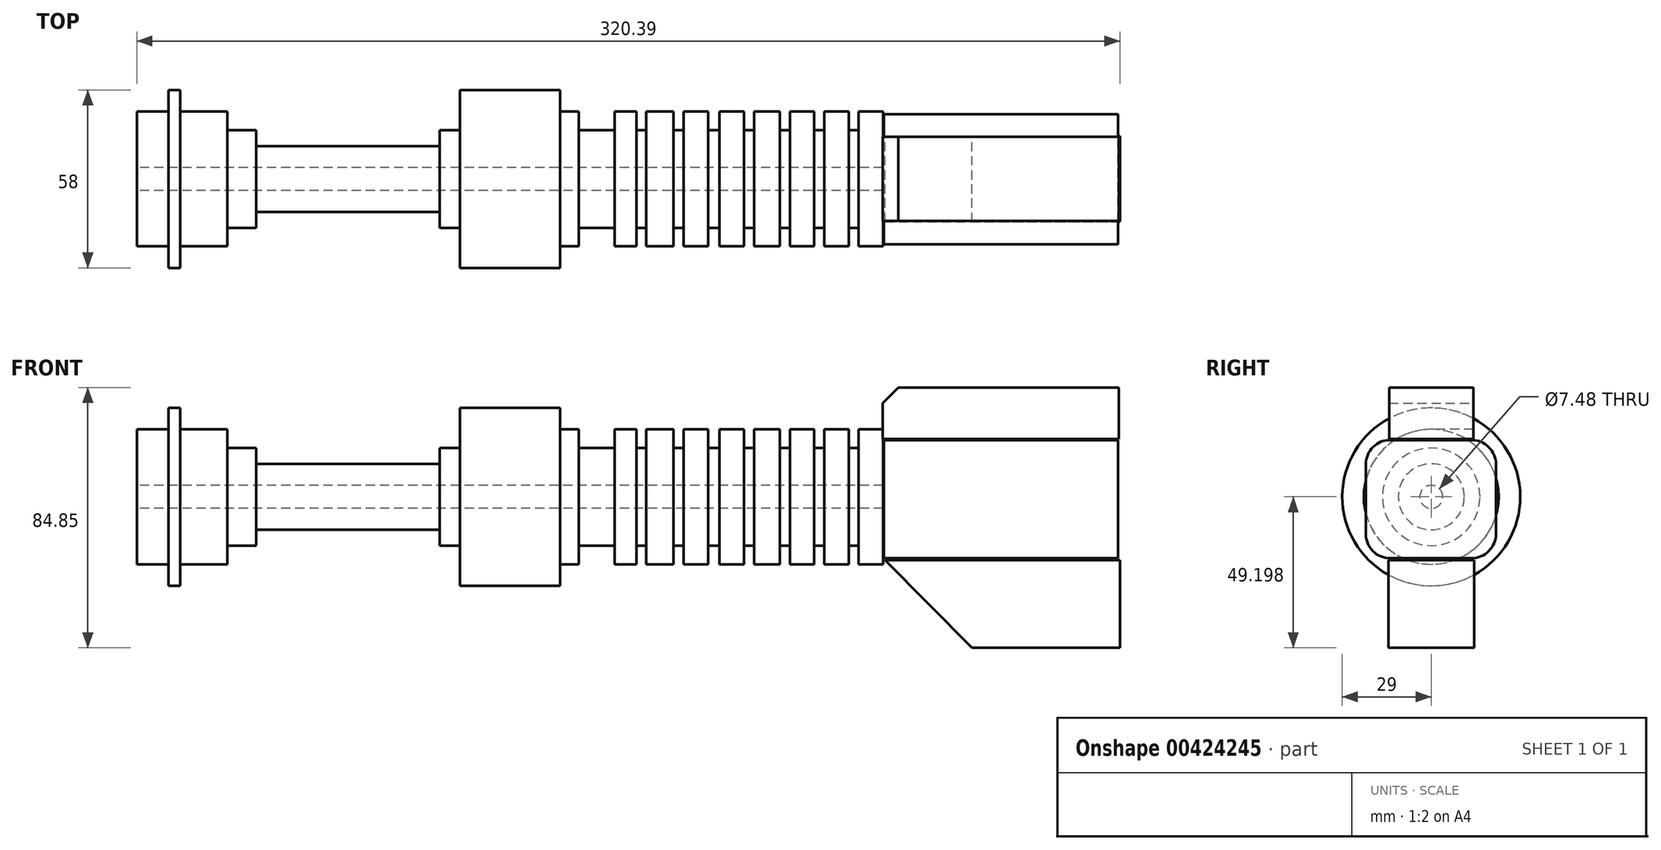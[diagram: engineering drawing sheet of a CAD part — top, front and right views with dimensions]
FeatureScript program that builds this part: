
annotation { "Feature Type Name" : "Feature", "Feature Type Description" : "" }
export const myFeature = defineFeature(function(context is Context, id is Id, definition is map)
    precondition{}
    {
        {
            var Q0;
            Q0=qCreatedBy(makeId("Front.planeOp"),FACE);
            var sketch = newSketch(context, id + "F0", { "sketchPlane" : qUnion([Q0])});
            skLineSegment(sketch, "E0", {"start": v(-174.92, 0) * mm, "end": v(0, 0) * mm});
            skLineSegment(sketch, "E1", {"start": v(-174.92, 0) * mm, "end": v(-174.92, 18.24) * mm});
            skLineSegment(sketch, "E2", {"start": v(-174.92, 18.24) * mm, "end": v(-164.63, 18.24) * mm});
            skLineSegment(sketch, "E3", {"start": v(-164.63, 18.24) * mm, "end": v(-164.63, 25.26) * mm});
            skLineSegment(sketch, "E4", {"start": v(-164.63, 25.26) * mm, "end": v(-160.89, 25.26) * mm});
            skLineSegment(sketch, "E5", {"start": v(-160.89, 25.26) * mm, "end": v(-160.89, 18.24) * mm});
            skLineSegment(sketch, "E6", {"start": v(-160.89, 18.24) * mm, "end": v(-145.45, 18.24) * mm});
            skLineSegment(sketch, "E7", {"start": v(-145.45, 18.24) * mm, "end": v(-145.45, 12.16) * mm});
            skLineSegment(sketch, "E8", {"start": v(-145.45, 12.16) * mm, "end": v(-136.1, 12.16) * mm});
            skLineSegment(sketch, "E9", {"start": v(-136.1, 12.16) * mm, "end": v(-136.1, 7.02) * mm});
            skLineSegment(sketch, "E10", {"start": v(-136.1, 7.02) * mm, "end": v(-76.23, 7.02) * mm});
            skLineSegment(sketch, "E11", {"start": v(-76.23, 7.02) * mm, "end": v(-76.23, 12.16) * mm});
            skLineSegment(sketch, "E12", {"start": v(-76.23, 12.16) * mm, "end": v(-69.69, 12.16) * mm});
            skLineSegment(sketch, "E13", {"start": v(-69.69, 12.16) * mm, "end": v(-69.69, 25.26) * mm});
            skLineSegment(sketch, "E14", {"start": v(-69.69, 25.26) * mm, "end": v(-36.95, 25.26) * mm});
            skLineSegment(sketch, "E15", {"start": v(-36.95, 25.26) * mm, "end": v(-36.95, 18.24) * mm});
            skLineSegment(sketch, "E16", {"start": v(-36.95, 18.24) * mm, "end": v(-30.87, 18.24) * mm});
            skLineSegment(sketch, "E17", {"start": v(-30.87, 18.24) * mm, "end": v(-30.87, 12.16) * mm});
            skLineSegment(sketch, "E18", {"start": v(-30.87, 12.16) * mm, "end": v(-19.18, 12.16) * mm});
            skLineSegment(sketch, "E19", {"start": v(-19.18, 12.16) * mm, "end": v(-19.18, 18.24) * mm});
            skLineSegment(sketch, "E20", {"start": v(-19.18, 18.24) * mm, "end": v(-12.16, 18.24) * mm});
            skLineSegment(sketch, "E21", {"start": v(-12.16, 18.24) * mm, "end": v(-12.16, 12.16) * mm});
            skLineSegment(sketch, "E22", {"start": v(-12.16, 12.16) * mm, "end": v(-8.89, 12.16) * mm});
            skLineSegment(sketch, "E23", {"start": v(-8.89, 12.16) * mm, "end": v(-8.89, 18.24) * mm});
            skLineSegment(sketch, "E24", {"start": v(-8.89, 18.24) * mm, "end": v(0, 18.24) * mm});
            skLineSegment(sketch, "E25", {"start": v(0, 18.24) * mm, "end": v(0, 12.16) * mm});
            skLineSegment(sketch, "E26", {"start": v(0, 12.16) * mm, "end": v(3.27, 12.16) * mm});
            skLineSegment(sketch, "E27", {"start": v(3.27, 12.16) * mm, "end": v(3.27, 18.24) * mm});
            skLineSegment(sketch, "E28", {"start": v(3.27, 18.24) * mm, "end": v(11.22, 18.24) * mm});
            skLineSegment(sketch, "E29", {"start": v(11.22, 18.24) * mm, "end": v(11.22, 12.16) * mm});
            skLineSegment(sketch, "E30", {"start": v(11.22, 12.16) * mm, "end": v(14.97, 12.16) * mm});
            skLineSegment(sketch, "E31", {"start": v(14.97, 12.16) * mm, "end": v(14.97, 18.24) * mm});
            skLineSegment(sketch, "E32", {"start": v(14.97, 18.24) * mm, "end": v(22.92, 18.24) * mm});
            skLineSegment(sketch, "E33", {"start": v(22.92, 18.24) * mm, "end": v(22.92, 12.16) * mm});
            skLineSegment(sketch, "E34", {"start": v(22.92, 12.16) * mm, "end": v(26.2, 12.16) * mm});
            skLineSegment(sketch, "E35", {"start": v(26.2, 12.16) * mm, "end": v(26.2, 18.24) * mm});
            skLineSegment(sketch, "E36", {"start": v(26.2, 18.24) * mm, "end": v(34.6, 18.24) * mm});
            skLineSegment(sketch, "E37", {"start": v(34.6, 18.24) * mm, "end": v(34.6, 12.16) * mm});
            skLineSegment(sketch, "E38", {"start": v(34.6, 12.16) * mm, "end": v(37.88, 12.16) * mm});
            skLineSegment(sketch, "E39", {"start": v(37.88, 12.16) * mm, "end": v(37.88, 18.24) * mm});
            skLineSegment(sketch, "E40", {"start": v(37.88, 18.24) * mm, "end": v(45.83, 18.24) * mm});
            skLineSegment(sketch, "E41", {"start": v(45.83, 18.24) * mm, "end": v(45.83, 12.16) * mm});
            skLineSegment(sketch, "E42", {"start": v(45.83, 12.16) * mm, "end": v(49.1, 12.16) * mm});
            skLineSegment(sketch, "E43", {"start": v(49.1, 12.16) * mm, "end": v(49.1, 18.24) * mm});
            skLineSegment(sketch, "E44", {"start": v(49.1, 18.24) * mm, "end": v(57.06, 18.24) * mm});
            skLineSegment(sketch, "E45", {"start": v(57.06, 18.24) * mm, "end": v(57.06, 12.16) * mm});
            skLineSegment(sketch, "E46", {"start": v(57.06, 12.16) * mm, "end": v(60.33, 12.16) * mm});
            skLineSegment(sketch, "E47", {"start": v(60.33, 12.16) * mm, "end": v(60.33, 18.24) * mm});
            skLineSegment(sketch, "E48", {"start": v(60.33, 18.24) * mm, "end": v(68.28, 18.24) * mm});
            skLineSegment(sketch, "E49", {"start": v(68.28, 18.24) * mm, "end": v(68.28, 12.16) * mm});
            skLineSegment(sketch, "E50", {"start": v(68.28, 12.16) * mm, "end": v(68.28, 0) * mm});
            skLineSegment(sketch, "E51", {"start": v(68.28, 0) * mm, "end": v(0, 0) * mm});
            skLineSegment(sketch, "E52", {"start": v(0, 0) * mm, "end": v(68.28, 0) * mm});
            skLineSegment(sketch, "E53", {"start": v(68.28, 0) * mm, "end": v(-174.92, 0) * mm});
            skLineSegment(sketch, "E54", {"start": v(-192.22, -3.74) * mm, "end": v(98.68, -3.74) * mm});
            skSolve(sketch);
        }
        {
            var Q0;
            {var subQ0=sQuery(id+"F0.wireOp",EDGE,"E1");Q0=makeQuery(id+"F0.imprint","IMPRINT",FACE,{"disambiguationData":[TD([[makeQuery(id+"F0.imprint","IMPRINT",EDGE,{"derivedFrom":subQ0}),-1.0]])]});}
            var Q1;
            Q1=sQuery(id+"F0.wireOp",EDGE,"E54");
            revolve(context, id + "F1", {"entities" : qUnion([Q0]), "axis" : qUnion([Q1]), "revolveType" : RevolveType.FULL});
        }
        {
            var Q0;
            Q0=qCreatedBy(makeId("Front.planeOp"),FACE);
            var sketch = newSketch(context, id + "F2", { "sketchPlane" : qUnion([Q0])});
            skLineSegment(sketch, "E55.bottom", {"start": v(68.52, 11.23) * mm, "end": v(144.82, 11.23) * mm});
            skLineSegment(sketch, "E55.top", {"start": v(68.52, -18.2) * mm, "end": v(144.82, -18.2) * mm});
            skLineSegment(sketch, "E55.left", {"start": v(68.52, 11.23) * mm, "end": v(68.52, -18.2) * mm});
            skLineSegment(sketch, "E55.right", {"start": v(144.82, 11.23) * mm, "end": v(144.82, -18.2) * mm});
            skSolve(sketch);
        }
        {
            var Q0;
            Q0 = qSketchRegion(id + "F2", true);
            extrude(context, id + "F3", {"entities" : qUnion([Q0]), "depth" : 21.34 * mm});
        }
        {
            var Q0;
            Q0=makeQuery(id+"F3.opExtrude","CAP_FACE",FACE,{"disambiguationData":[OSD([sQuery(id+"F2.wireOp",EDGE,"E55.bottom"),sQuery(id+"F2.wireOp",EDGE,"E55.top"),sQuery(id+"F2.wireOp",EDGE,"E55.left"),sQuery(id+"F2.wireOp",EDGE,"E55.right")])],"isStart":true});
            extrude(context, id + "F4", {"entities" : qUnion([Q0]), "operationType" : NewBodyOperationType.ADD, "depth" : 21.08 * mm});
        }
        {
            var Q0;
            {var subQ0=sQuery(id+"F2.wireOp",EDGE,"E55.bottom");Q0=makeQuery(id+"F4.boolean.opBoolean","MERGE",FACE,{"derivedFrom":[makeQuery(id+"F3.opExtrude","SWEPT_FACE",FACE,{"disambiguationData":[OSD([subQ0])]}),makeQuery(id+"F4.opExtrude","SWEPT_FACE",FACE,{"disambiguationData":[OSD([subQ0])]})]});}
            extrude(context, id + "F5", {"entities" : qUnion([Q0]), "operationType" : NewBodyOperationType.ADD, "depth" : 3.56 * mm});
        }
        {
            var Q0;
            {var subQ0=sQuery(id+"F2.wireOp",EDGE,"E55.top");Q0=makeQuery(id+"F4.boolean.opBoolean","MERGE",FACE,{"derivedFrom":[makeQuery(id+"F3.opExtrude","SWEPT_FACE",FACE,{"disambiguationData":[OSD([subQ0])]}),makeQuery(id+"F4.opExtrude","SWEPT_FACE",FACE,{"disambiguationData":[OSD([subQ0])]})]});}
            extrude(context, id + "F6", {"entities" : qUnion([Q0]), "operationType" : NewBodyOperationType.ADD, "depth" : 5.6 * mm});
        }
        {
            var Q0;
            {var subQ0=sQuery(id+"F2.wireOp",EDGE,"E55.top");Q0=makeQuery(id+"F6.opExtrude","CAP_EDGE",EDGE,{"disambiguationData":[OSD([subQ0]),TDD([makeQuery(id+"F3.opExtrude","CAP_EDGE",EDGE,{"disambiguationData":[OSD([subQ0])],"isStart":false})])],"isStart":false});}
            fillet(context, id + "F7", {"entities" : qUnion([Q0]), "radius" : 7.97 * mm, "tangentPropagation" : true, "allowEdgeOverflow" : false});
        }
        {
            var Q0;
            {var subQ0=sQuery(id+"F2.wireOp",EDGE,"E55.bottom");Q0=makeQuery(id+"F5.opExtrude","CAP_EDGE",EDGE,{"disambiguationData":[OSD([subQ0]),TDD([makeQuery(id+"F3.opExtrude","CAP_EDGE",EDGE,{"disambiguationData":[OSD([subQ0])],"isStart":false})])],"isStart":false});}
            fillet(context, id + "F8", {"entities" : qUnion([Q0]), "radius" : 7.98 * mm, "tangentPropagation" : true, "allowEdgeOverflow" : false});
        }
        {
            var Q0;
            {var subQ0=sQuery(id+"F2.wireOp",EDGE,"E55.bottom");Q0=makeQuery(id+"F5.opExtrude","CAP_EDGE",EDGE,{"disambiguationData":[OSD([subQ0]),TDD([makeQuery(id+"F4.opExtrude","CAP_EDGE",EDGE,{"disambiguationData":[OSD([subQ0])],"isStart":false})])],"isStart":false});}
            fillet(context, id + "F9", {"entities" : qUnion([Q0]), "radius" : 7.98 * mm, "tangentPropagation" : true, "allowEdgeOverflow" : false});
        }
        {
            var Q0;
            {var subQ0=sQuery(id+"F2.wireOp",EDGE,"E55.top");Q0=makeQuery(id+"F6.opExtrude","CAP_EDGE",EDGE,{"disambiguationData":[OSD([subQ0]),TDD([makeQuery(id+"F4.opExtrude","CAP_EDGE",EDGE,{"disambiguationData":[OSD([subQ0])],"isStart":false})])],"isStart":false});}
            fillet(context, id + "F10", {"entities" : qUnion([Q0]), "radius" : 7.98 * mm, "tangentPropagation" : true, "allowEdgeOverflow" : false});
        }
        {
            var Q0;
            Q0=qCreatedBy(makeId("Front.planeOp"),FACE);
            var sketch = newSketch(context, id + "F11", { "sketchPlane" : qUnion([Q0])});
            skLineSegment(sketch, "E56.bottom", {"start": v(68.2, 15.1) * mm, "end": v(145.12, 15.1) * mm});
            skLineSegment(sketch, "E56.top", {"start": v(68.2, 31.9) * mm, "end": v(145.12, 31.9) * mm});
            skLineSegment(sketch, "E56.left", {"start": v(68.2, 15.1) * mm, "end": v(68.2, 31.9) * mm});
            skLineSegment(sketch, "E56.right", {"start": v(145.12, 15.1) * mm, "end": v(145.12, 31.9) * mm});
            skSolve(sketch);
        }
        {
            var Q0;
            Q0=makeQuery(id+"F11.imprint","IMPRINT",FACE,{"disambiguationData":[TD([[makeQuery(id+"F11.imprint","IMPRINT",EDGE,{"derivedFrom":sQuery(id+"F11.wireOp",EDGE,"E56.bottom")}),1.0]])]});
            extrude(context, id + "F12", {"entities" : qUnion([Q0]), "operationType" : NewBodyOperationType.ADD, "depth" : 13.72 * mm});
        }
        {
            var Q0;
            Q0=makeQuery(id+"F12.opExtrude","CAP_FACE",FACE,{"disambiguationData":[OSD([sQuery(id+"F11.wireOp",EDGE,"E56.bottom"),sQuery(id+"F11.wireOp",EDGE,"E56.top"),sQuery(id+"F11.wireOp",EDGE,"E56.left"),sQuery(id+"F11.wireOp",EDGE,"E56.right")])],"isStart":true});
            extrude(context, id + "F13", {"entities" : qUnion([Q0]), "operationType" : NewBodyOperationType.ADD, "depth" : 13.72 * mm});
        }
        {
            var Q0;
            {var subQ0=sQuery(id+"F11.wireOp",EDGE,"E56.left");var subQ1=sQuery(id+"F11.wireOp",EDGE,"E56.top");Q0=makeQuery(id+"F13.boolean.opBoolean","MERGE",EDGE,{"derivedFrom":[makeQuery(id+"F12.opExtrude","SWEPT_EDGE",EDGE,{"disambiguationData":[OSD([subQ1,subQ0])]}),makeQuery(id+"F13.opExtrude","SWEPT_EDGE",EDGE,{"disambiguationData":[OSD([subQ1,subQ0])]})]});}
            chamfer(context, id + "F14", {"entities" : qUnion([Q0]), "width" : 5.08 * mm, "tangentPropagation" : true});
        }
        {
            var Q0;
            Q0=qCreatedBy(makeId("Front.planeOp"),FACE);
            var sketch = newSketch(context, id + "F15", { "sketchPlane" : qUnion([Q0])});
            skLineSegment(sketch, "E57", {"start": v(68.97, -24.34) * mm, "end": v(97.2, -52.94) * mm});
            skLineSegment(sketch, "E58", {"start": v(97.2, -52.94) * mm, "end": v(145.47, -52.94) * mm});
            skLineSegment(sketch, "E59", {"start": v(145.47, -52.94) * mm, "end": v(145.47, 14.62) * mm});
            skLineSegment(sketch, "E60", {"start": v(68.97, -24.34) * mm, "end": v(145.47, -24.34) * mm});
            skSolve(sketch);
        }
        {
            var Q0;
            Q0=makeQuery(id+"F15.imprint","IMPRINT",FACE,{"disambiguationData":[TD([[makeQuery(id+"F15.imprint","IMPRINT",EDGE,{"derivedFrom":sQuery(id+"F15.wireOp",EDGE,"E57")}),1.0]])]});
            extrude(context, id + "F16", {"entities" : qUnion([Q0]), "depth" : 13.97 * mm});
        }
        {
            var Q0;
            Q0=makeQuery(id+"F16.opExtrude","CAP_FACE",FACE,{"disambiguationData":[OSD([sQuery(id+"F15.wireOp",EDGE,"E57"),sQuery(id+"F15.wireOp",EDGE,"E58"),sQuery(id+"F15.wireOp",EDGE,"E59"),sQuery(id+"F15.wireOp",EDGE,"E60")])],"isStart":true});
            extrude(context, id + "F17", {"entities" : qUnion([Q0]), "operationType" : NewBodyOperationType.ADD, "depth" : 13.97 * mm});
        }
        {
            var Q0;
            Q0=qCreatedBy(makeId("Front.planeOp"),FACE);
            var sketch = newSketch(context, id + "F18", { "sketchPlane" : qUnion([Q0])});
            skLineSegment(sketch, "E61", {"start": v(144.05, 15.18) * mm, "end": v(232.8, 15.18) * mm});
            skLineSegment(sketch, "E62", {"start": v(144.75, -5.24) * mm, "end": v(284.92, -5.24) * mm});
            skSolve(sketch);
        }
        {
            var Q0;
            Q0=sQuery(id+"F18.wireOp",EDGE,"E61");
            var Q1;
            Q1=sQuery(id+"F18.wireOp",EDGE,"E62");
            revolve(context, id + "F19", {"bodyType" : ToolBodyType.SURFACE, "surfaceEntities" : qUnion([Q0]), "axis" : qUnion([Q1]), "revolveType" : RevolveType.FULL});
        }
    });
